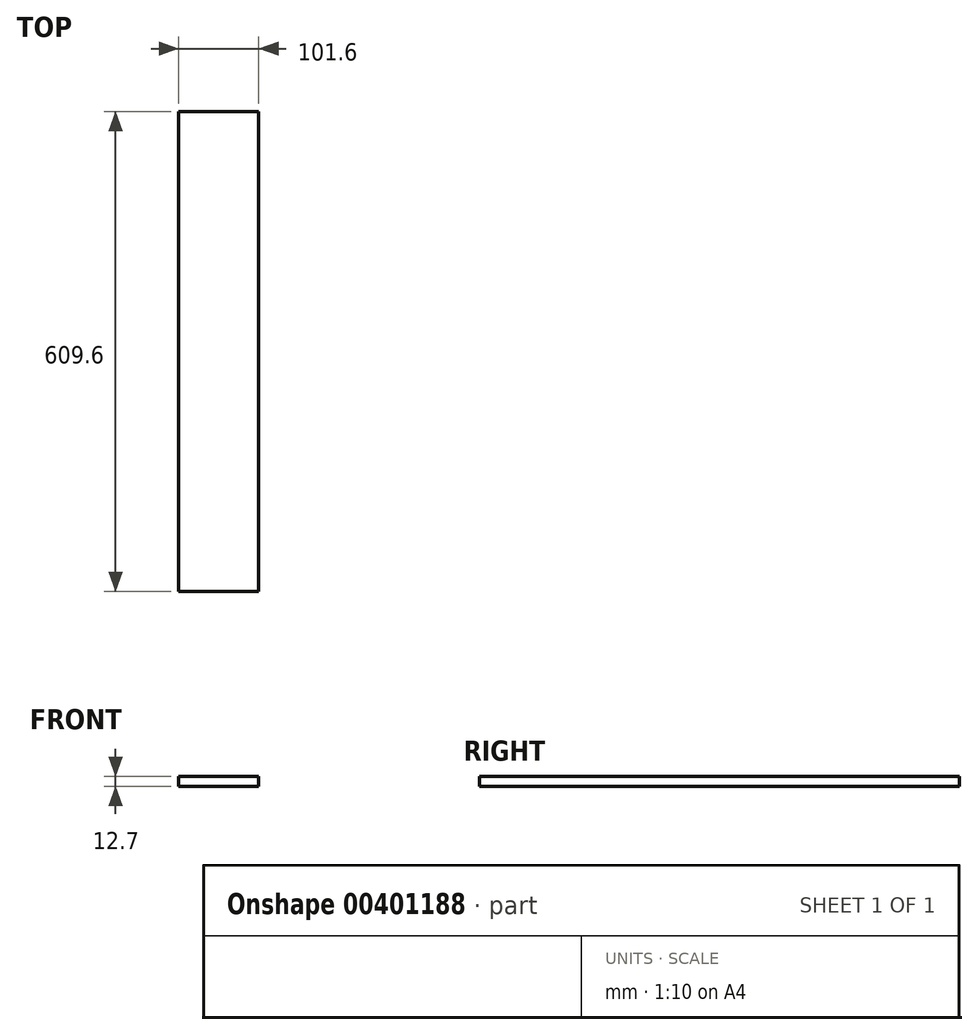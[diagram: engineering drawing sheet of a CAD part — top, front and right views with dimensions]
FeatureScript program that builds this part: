
annotation { "Feature Type Name" : "Feature", "Feature Type Description" : "" }
export const myFeature = defineFeature(function(context is Context, id is Id, definition is map)
    precondition{}
    {
        {
            var Q0;
            Q0=qCreatedBy(makeId("Front.planeOp"),FACE);
            var sketch = newSketch(context, id + "F0", { "sketchPlane" : qUnion([Q0])});
            skLineSegment(sketch, "E0.bottom", {"start": v(0, 0) * mm, "end": v(-101.6, 0) * mm});
            skLineSegment(sketch, "E0.top", {"start": v(0, 12.7) * mm, "end": v(-101.6, 12.7) * mm});
            skLineSegment(sketch, "E0.left", {"start": v(0, 0) * mm, "end": v(0, 12.7) * mm});
            skLineSegment(sketch, "E0.right", {"start": v(-101.6, 0) * mm, "end": v(-101.6, 12.7) * mm});
            skSolve(sketch);
        }
        {
            var Q0;
            Q0=makeQuery(id+"F0.imprint","IMPRINT",FACE,{"disambiguationData":[TD([[makeQuery(id+"F0.imprint","IMPRINT",EDGE,{"derivedFrom":sQuery(id+"F0.wireOp",EDGE,"E0.bottom")}),-1.0]])]});
            extrude(context, id + "F1", {"entities" : qUnion([Q0]), "depth" : 609.6 * mm});
        }
    });
